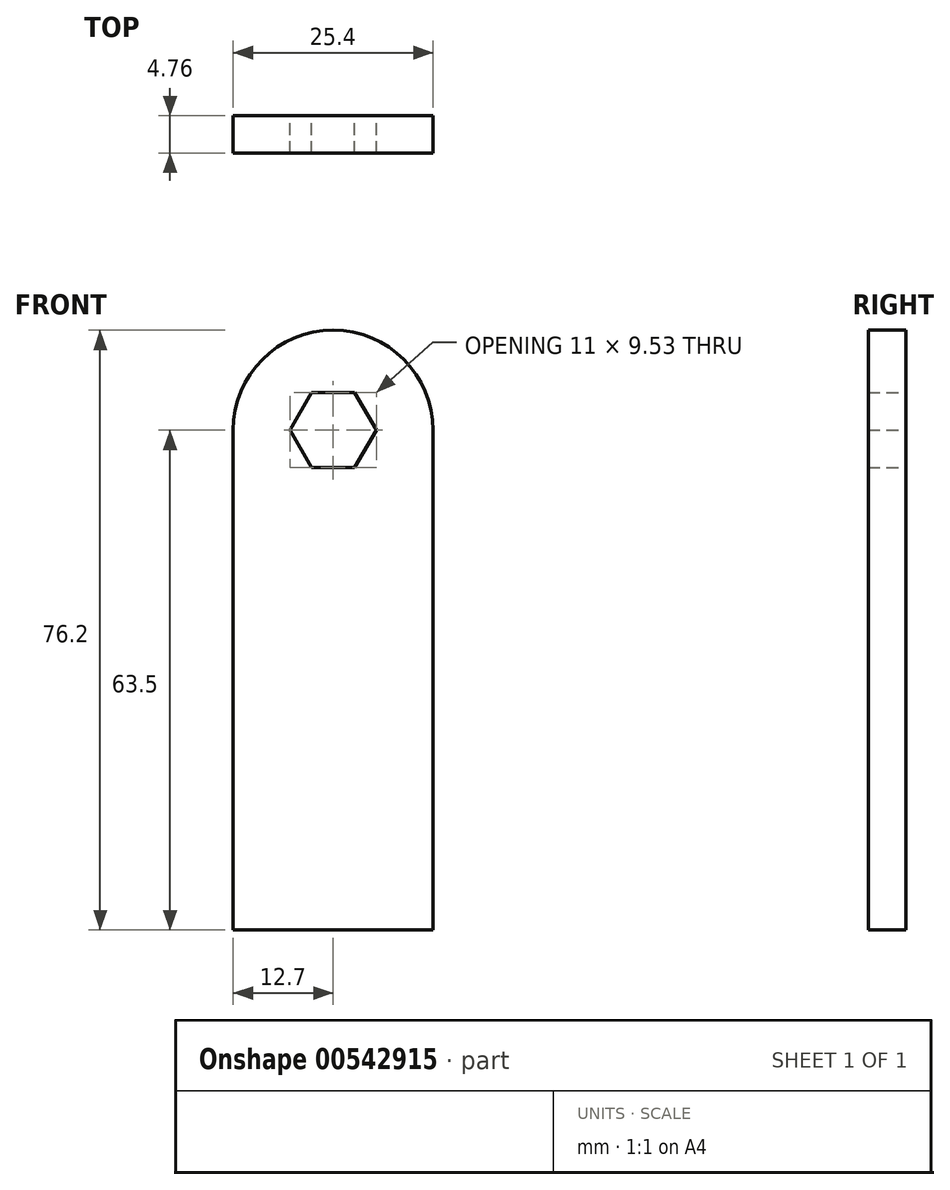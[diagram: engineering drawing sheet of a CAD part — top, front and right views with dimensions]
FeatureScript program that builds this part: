
annotation { "Feature Type Name" : "Feature", "Feature Type Description" : "" }
export const myFeature = defineFeature(function(context is Context, id is Id, definition is map)
    precondition{}
    {
        {
            var Q0;
            Q0=qCreatedBy(makeId("Front.planeOp"),FACE);
            var sketch = newSketch(context, id + "F0", { "sketchPlane" : qUnion([Q0])});
            skLineSegment(sketch, "E0", {"start": v(0, 0) * mm, "end": v(0, 63.5) * mm});
            skLineSegment(sketch, "E1", {"start": v(0, 0) * mm, "end": v(25.4, 0) * mm});
            skLineSegment(sketch, "E2", {"start": v(25.4, 0) * mm, "end": v(25.4, 63.5) * mm});
            skPoint(sketch, "E3.center.orphan", {"position": v(12.7, 63.5) * mm});
            skArc(sketch, "E4", {"start": v(25.4, 63.5) * mm, "mid": v(12.7, 76.2) * mm, "end": v(0, 63.5) * mm});
            skCircle(sketch, "E5.cCircle", {"center": v(12.7, 63.5) * mm, "radius": 4.76 * mm, "construction": true});
            skLineSegment(sketch, "E5.0", {"start": v(9.95, 68.26) * mm, "end": v(15.45, 68.26) * mm});
            skLineSegment(sketch, "E5.1", {"start": v(15.45, 68.26) * mm, "end": v(18.2, 63.5) * mm});
            skLineSegment(sketch, "E5.2", {"start": v(18.2, 63.5) * mm, "end": v(15.45, 58.74) * mm});
            skLineSegment(sketch, "E5.3", {"start": v(15.45, 58.74) * mm, "end": v(9.95, 58.74) * mm});
            skLineSegment(sketch, "E5.4", {"start": v(9.95, 58.74) * mm, "end": v(7.2, 63.5) * mm});
            skLineSegment(sketch, "E5.5", {"start": v(7.2, 63.5) * mm, "end": v(9.95, 68.26) * mm});
            skPoint(sketch, "E5.0.midPoint", {"position": v(12.7, 68.26) * mm});
            skSolve(sketch);
        }
        {
            var Q0;
            Q0=makeQuery(id+"F0.imprint","IMPRINT",FACE,{"disambiguationData":[TD([[makeQuery(id+"F0.imprint","IMPRINT",EDGE,{"derivedFrom":sQuery(id+"F0.wireOp",EDGE,"E0")}),-1.0]])]});
            extrude(context, id + "F1", {"entities" : qUnion([Q0]), "depth" : 4.76 * mm, "offsetDistance" : 25.4 * mm});
        }
    });
